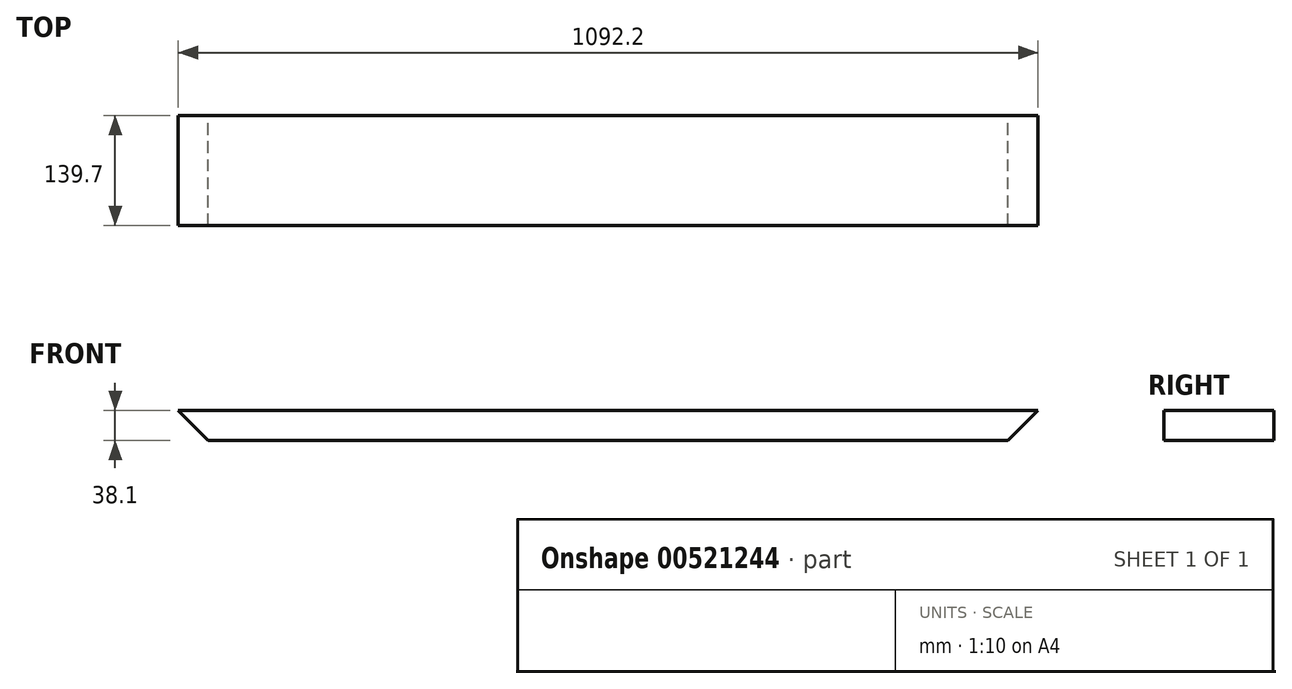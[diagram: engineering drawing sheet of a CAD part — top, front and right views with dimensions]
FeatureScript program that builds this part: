
annotation { "Feature Type Name" : "Feature", "Feature Type Description" : "" }
export const myFeature = defineFeature(function(context is Context, id is Id, definition is map)
    precondition{}
    {
        {
            var Q0;
            Q0=qCreatedBy(makeId("Front.planeOp"),FACE);
            var sketch = newSketch(context, id + "F0", { "sketchPlane" : qUnion([Q0])});
            skLineSegment(sketch, "E0", {"start": v(-508, 0) * mm, "end": v(-546.1, 38.1) * mm});
            skLineSegment(sketch, "E1", {"start": v(-546.1, 38.1) * mm, "end": v(546.1, 38.1) * mm});
            skLineSegment(sketch, "E2", {"start": v(546.1, 38.1) * mm, "end": v(508, 0) * mm});
            skLineSegment(sketch, "E3", {"start": v(508, 0) * mm, "end": v(-508, 0) * mm});
            skLineSegment(sketch, "E4", {"start": v(0, 570.25) * mm, "end": v(0, -656.25) * mm});
            skLineSegment(sketch, "E5", {"start": v(-542.33, 0) * mm, "end": v(651.2, 0) * mm});
            skSolve(sketch);
        }
        {
            var Q0;
            {var subQ0=sQuery(id+"F0.wireOp",EDGE,"E2");Q0=makeQuery(id+"F0.imprint","IMPRINT",FACE,{"disambiguationData":[TD([[makeQuery(id+"F0.imprint","IMPRINT",EDGE,{"derivedFrom":subQ0}),-1.0]])]});}
            var Q1;
            {var subQ0=sQuery(id+"F0.wireOp",EDGE,"E0");Q1=makeQuery(id+"F0.imprint","IMPRINT",FACE,{"disambiguationData":[TD([[makeQuery(id+"F0.imprint","IMPRINT",EDGE,{"derivedFrom":subQ0}),-1.0]])]});}
            extrude(context, id + "F1", {"entities" : qUnion([Q0, Q1]), "depth" : 139.7 * mm, "offsetDistance" : 25.4 * mm});
        }
    });
